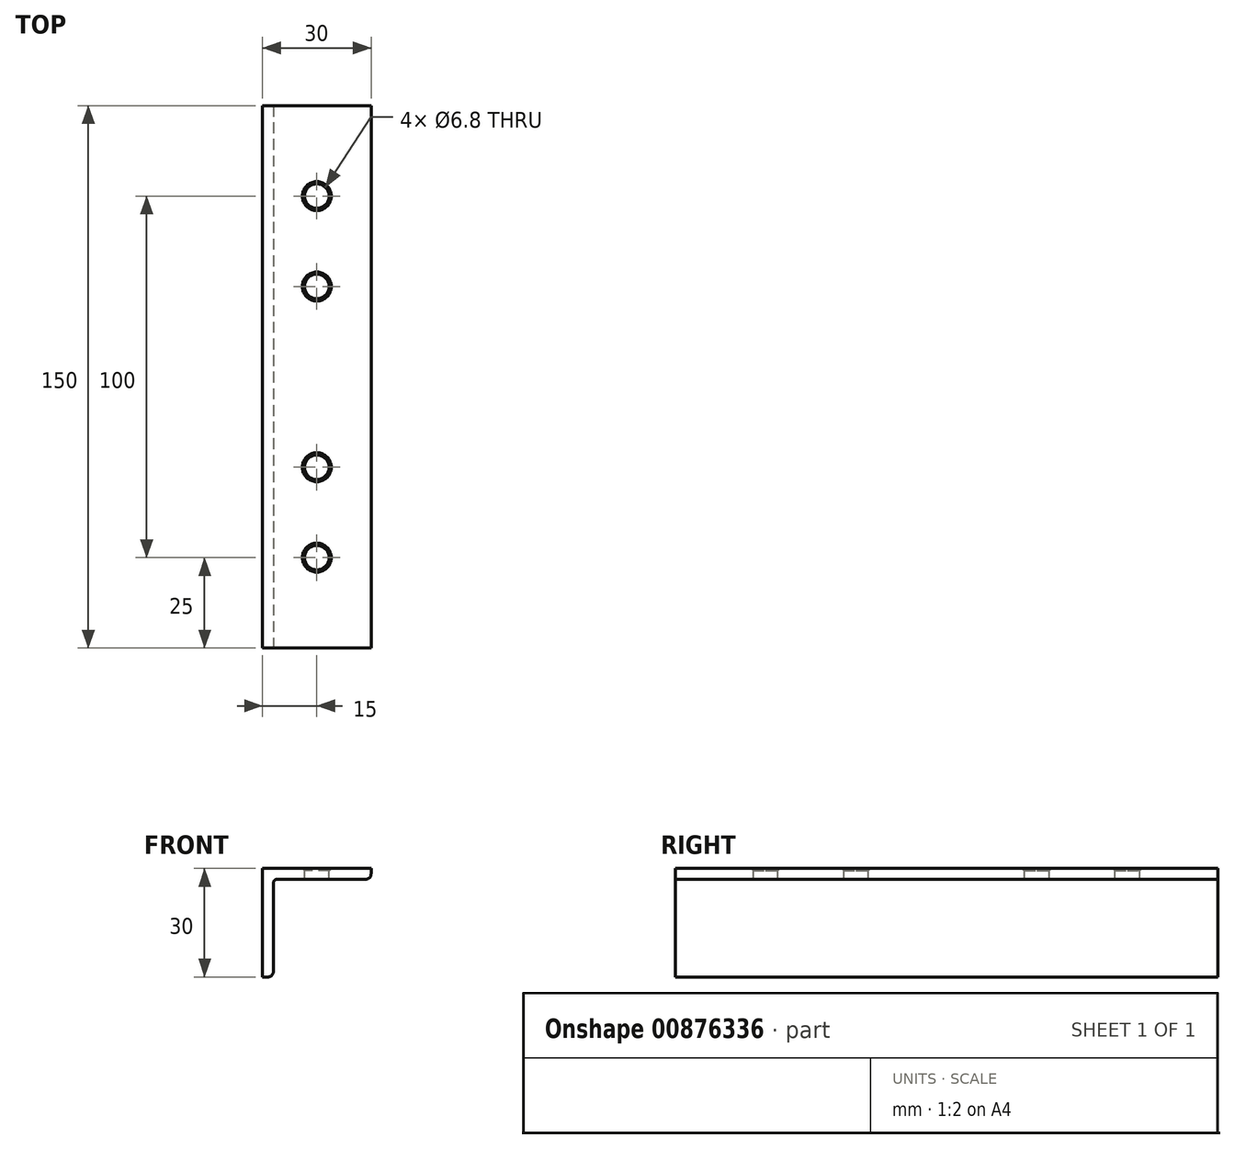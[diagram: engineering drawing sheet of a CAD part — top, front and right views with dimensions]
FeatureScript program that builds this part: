
annotation { "Feature Type Name" : "Feature", "Feature Type Description" : "" }
export const myFeature = defineFeature(function(context is Context, id is Id, definition is map)
    precondition{}
    {
        {
            var Q0;
            Q0=qCreatedBy(makeId("Front.planeOp"),FACE);
            var sketch = newSketch(context, id + "F0", { "sketchPlane" : qUnion([Q0])});
            skLineSegment(sketch, "E0", {"start": v(0, 0) * mm, "end": v(30, 0) * mm});
            skLineSegment(sketch, "E1", {"start": v(30, 0) * mm, "end": v(30, -1.5) * mm});
            skLineSegment(sketch, "E2", {"start": v(28.5, -3) * mm, "end": v(4, -3) * mm});
            skLineSegment(sketch, "E3", {"start": v(3, -4) * mm, "end": v(3, -28.5) * mm});
            skLineSegment(sketch, "E4", {"start": v(1.5, -30) * mm, "end": v(0, -30) * mm});
            skLineSegment(sketch, "E5", {"start": v(0, -30) * mm, "end": v(0, 0) * mm});
            skPoint(sketch, "E6.visualSharp", {"position": v(30, -3) * mm});
            skArc(sketch, "E6.filletArc", {"start": v(28.5, -3) * mm, "mid": v(29.56, -2.56) * mm, "end": v(30, -1.5) * mm});
            skPoint(sketch, "E7.visualSharp", {"position": v(3, -30) * mm});
            skArc(sketch, "E7.filletArc", {"start": v(1.5, -30) * mm, "mid": v(2.56, -29.56) * mm, "end": v(3, -28.5) * mm});
            skPoint(sketch, "E8.visualSharp", {"position": v(3, -3) * mm});
            skArc(sketch, "E8.filletArc", {"start": v(4, -3) * mm, "mid": v(3.3, -3.3) * mm, "end": v(3, -4) * mm});
            skSolve(sketch);
        }
        {
            var Q0;
            Q0=qCreatedBy(makeId("Right.planeOp"),FACE);
            var sketch = newSketch(context, id + "F1", { "sketchPlane" : qUnion([Q0])});
            skLineSegment(sketch, "E9", {"start": v(0, 0) * mm, "end": v(-150, 0) * mm});
            skSolve(sketch);
        }
        {
            var Q0;
            Q0=makeQuery(id+"F0.imprint","IMPRINT",FACE,{"disambiguationData":[TD([[makeQuery(id+"F0.imprint","IMPRINT",EDGE,{"derivedFrom":sQuery(id+"F0.wireOp",EDGE,"E0")}),-1.0]])]});
            var Q1;
            Q1=sQuery(id+"F1.wireOp",EDGE,"E9");
            sweep(context, id + "F2", {"profiles" : qUnion([Q0]), "path" : qUnion([Q1])});
        }
        {
            var Q0;
            Q0=qCreatedBy(makeId("Top.planeOp"),FACE);
            var sketch = newSketch(context, id + "F3", { "sketchPlane" : qUnion([Q0])});
            skCircle(sketch, "E10", {"center": v(15, -25) * mm, "radius": 4.5 * mm});
            skCircle(sketch, "E11", {"center": v(15, -125) * mm, "radius": 4.5 * mm});
            skCircle(sketch, "E12", {"center": v(15, -100) * mm, "radius": 4.5 * mm});
            skCircle(sketch, "E13", {"center": v(15, -50) * mm, "radius": 4.5 * mm});
            skSolve(sketch);
        }
        {
            var Q0;
            Q0=sQuery(id+"F3.wireOp",VERTEX,"E11.center");
            var Q1;
            Q1=sQuery(id+"F3.wireOp",VERTEX,"E10.center");
            var Q2;
            Q2=sQuery(id+"F3.wireOp",VERTEX,"E12.center");
            var Q3;
            Q3=sQuery(id+"F3.wireOp",VERTEX,"E13.center");
            var Q4;
            Q4=makeQuery(id+"F2.opSweep","SWEPT_BODY",BODY,{"disambiguationData":[OSD([sQuery(id+"F0.wireOp",EDGE,"E0"),sQuery(id+"F0.wireOp",EDGE,"E1"),sQuery(id+"F0.wireOp",EDGE,"E2"),sQuery(id+"F0.wireOp",EDGE,"E3"),sQuery(id+"F0.wireOp",EDGE,"E4"),sQuery(id+"F0.wireOp",EDGE,"E5"),sQuery(id+"F0.wireOp",EDGE,"E6.filletArc"),sQuery(id+"F0.wireOp",EDGE,"E7.filletArc"),sQuery(id+"F0.wireOp",EDGE,"E8.filletArc"),sQuery(id+"F1.wireOp",EDGE,"E9")])]});
            hole(context, id + "F4", {"style" : HoleStyle.C_SINK, "endStyle" : HoleEndStyle.BLIND, "holeDiameter" : 6.8 * mm, "cSinkDiameter" : 8 * mm, "cSinkAngle" : 90 * degree, "majorDiameter" : 8 * mm, "holeDepth" : 5 * mm, "isTappedThrough" : true, "tappedDepth" : 4 * mm, "tapClearance" : 0, "locations" : qUnion([Q0, Q1, Q2, Q3]), "scope" : qUnion([Q4])});
        }
    });
